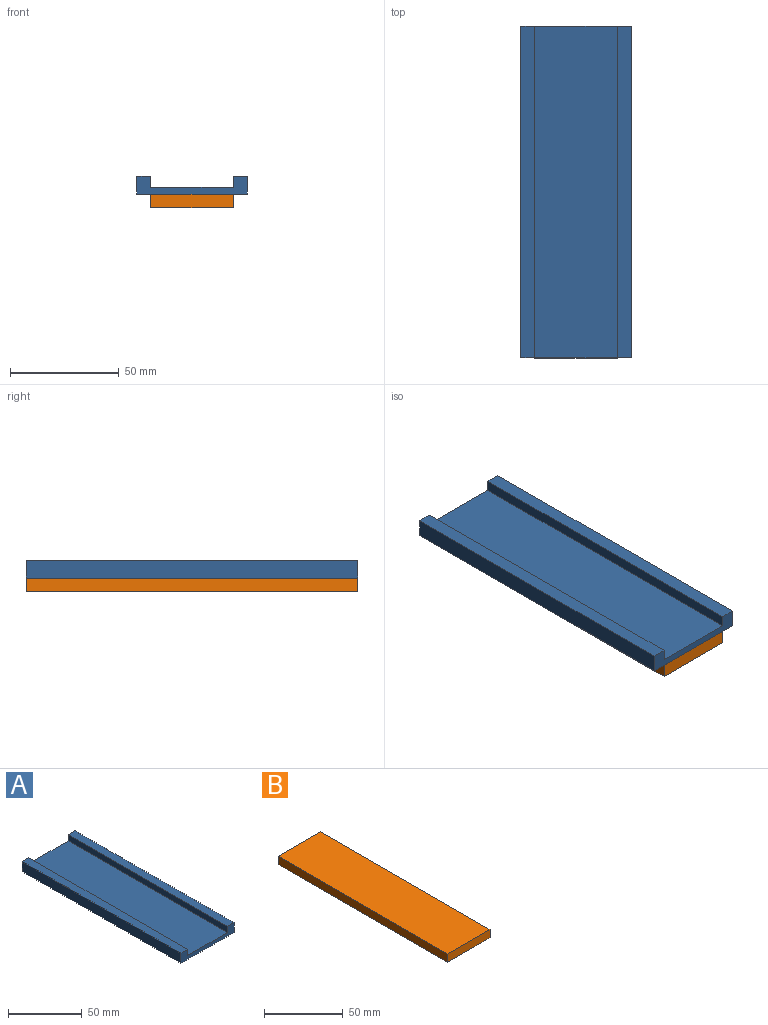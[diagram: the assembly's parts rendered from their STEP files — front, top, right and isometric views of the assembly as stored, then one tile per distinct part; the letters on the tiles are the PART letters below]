
ASSEMBLY  parts=2 mates=1
PART A: 10 faces, bbox 50.8x152.4x8.3 mm
  f0: plane 152.4x37.98mm, normal (0,0,1), area 5788.8mm2, adj f2,f4,f6,f8
  f1: plane 152.4x8.26mm, normal (-1,0,0), area 1258.1mm2, adj f2,f4,f5,f7
  f2: plane 50.8x8.26mm, normal (0,-1,0), area 226.4mm2, adj f0,f1,f3,f5,f6,f7,f8,f9
  f3: plane 152.4x8.26mm, normal (1,0,0), area 1258.1mm2, adj f2,f4,f5,f9
  f4: plane 50.8x8.26mm, normal (0,1,0), area 226.4mm2, adj f0,f1,f3,f5,f6,f7,f8,f9
  f5: plane 152.4x50.8mm, normal (0,0,-1), area 7741.9mm2, adj f1,f2,f3,f4
  f6: plane 152.4x5.08mm, normal (1,0,0), area 774.2mm2, adj f0,f2,f4,f7
  f7: plane 152.4x6.37mm, normal (0,0,1), area 970.4mm2, adj f1,f2,f4,f6
  f8: plane 152.4x5.08mm, normal (-1,0,0), area 774.2mm2, adj f0,f2,f4,f9
  f9: plane 152.4x6.45mm, normal (0,0,1), area 982.7mm2, adj f2,f3,f4,f8
PART B: 6 faces, bbox 38.1x152.4x6.4 mm
  f0: plane 152.4x6.35mm, normal (-1,0,0), area 967.7mm2, adj f1,f3,f4,f5
  f1: plane 38.1x6.35mm, normal (0,-1,0), area 241.9mm2, adj f0,f2,f4,f5
  f2: plane 152.4x6.35mm, normal (1,0,0), area 967.7mm2, adj f1,f3,f4,f5
  f3: plane 38.1x6.35mm, normal (0,1,0), area 241.9mm2, adj f0,f2,f4,f5
  f4: plane 152.4x38.1mm, normal (0,0,1), area 5806.4mm2, adj f0,f1,f2,f3
  f5: plane 152.4x38.1mm, normal (0,0,-1), area 5806.4mm2, adj f0,f1,f2,f3
PLACE A t=(-6.56,3.48,21.07)mm
PLACE B t=(-8.81,-7.93,14.72)mm
MATE fastened B.f4 <-> A.f5  axis (0,0,1) through (-17.47,6.71,21.07)mm
